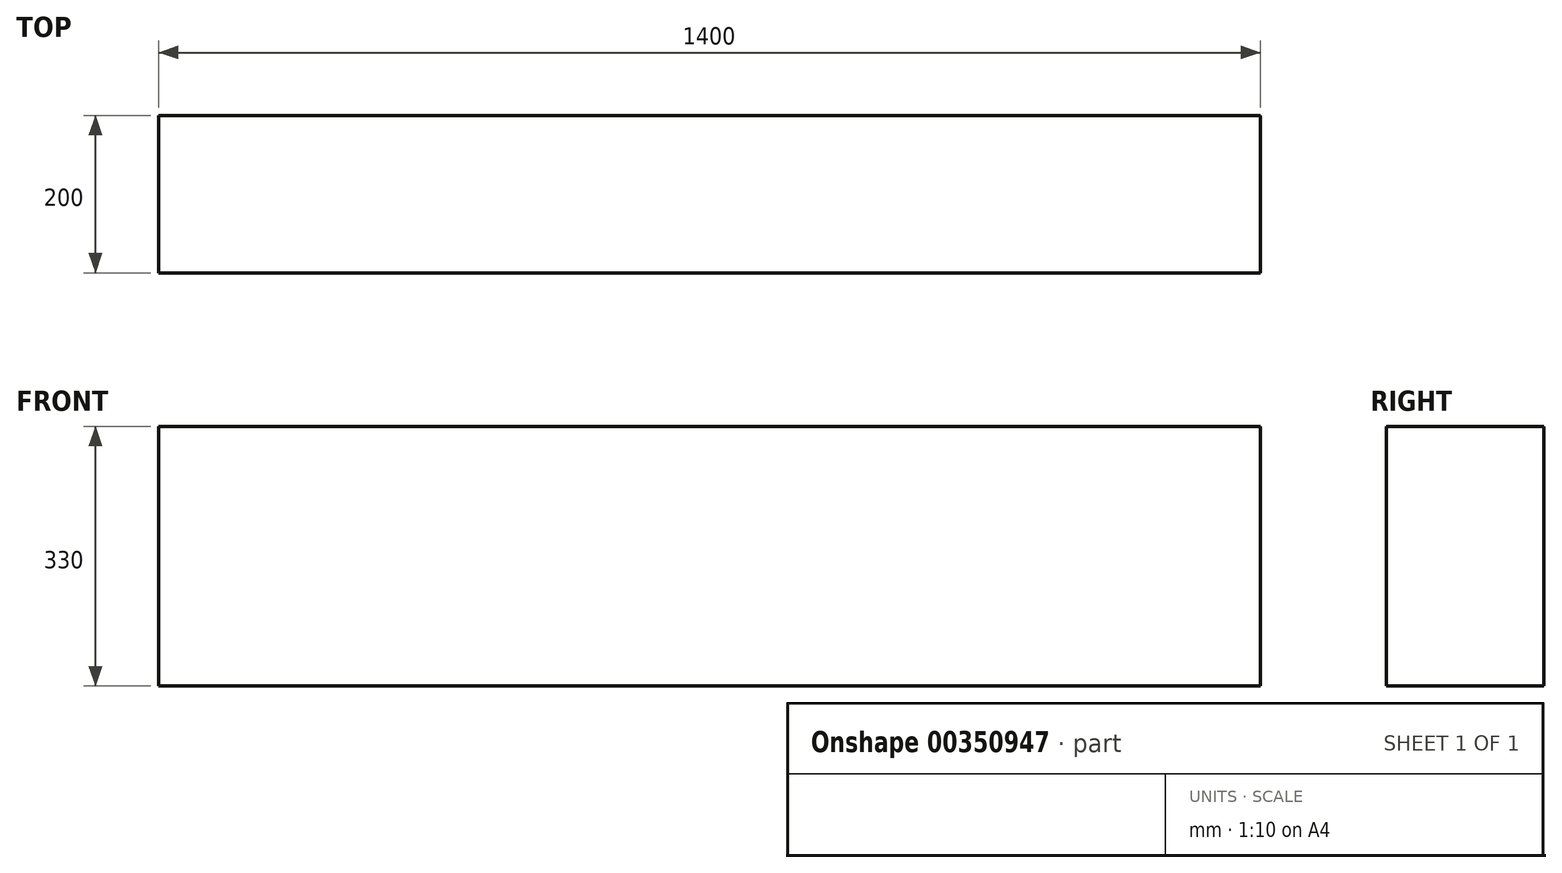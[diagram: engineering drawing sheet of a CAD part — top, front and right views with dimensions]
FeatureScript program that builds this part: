
annotation { "Feature Type Name" : "Feature", "Feature Type Description" : "" }
export const myFeature = defineFeature(function(context is Context, id is Id, definition is map)
    precondition{}
    {
        {
            var Q0;
            Q0=qCreatedBy(makeId("Front.planeOp"),FACE);
            var sketch = newSketch(context, id + "F0", { "sketchPlane" : qUnion([Q0])});
            skLineSegment(sketch, "E0.bottom", {"start": v(-700, 165) * mm, "end": v(700, 165) * mm});
            skLineSegment(sketch, "E0.top", {"start": v(-700, -165) * mm, "end": v(700, -165) * mm});
            skLineSegment(sketch, "E0.left", {"start": v(-700, 165) * mm, "end": v(-700, -165) * mm});
            skLineSegment(sketch, "E0.right", {"start": v(700, 165) * mm, "end": v(700, -165) * mm});
            skPoint(sketch, "E0.middle", {"position": v(0, 0) * mm});
            skSolve(sketch);
        }
        {
            var Q0;
            Q0 = qSketchRegion(id + "F0", true);
            extrude(context, id + "F1", {"entities" : qUnion([Q0]), "depth" : 200 * mm});
        }
    });
